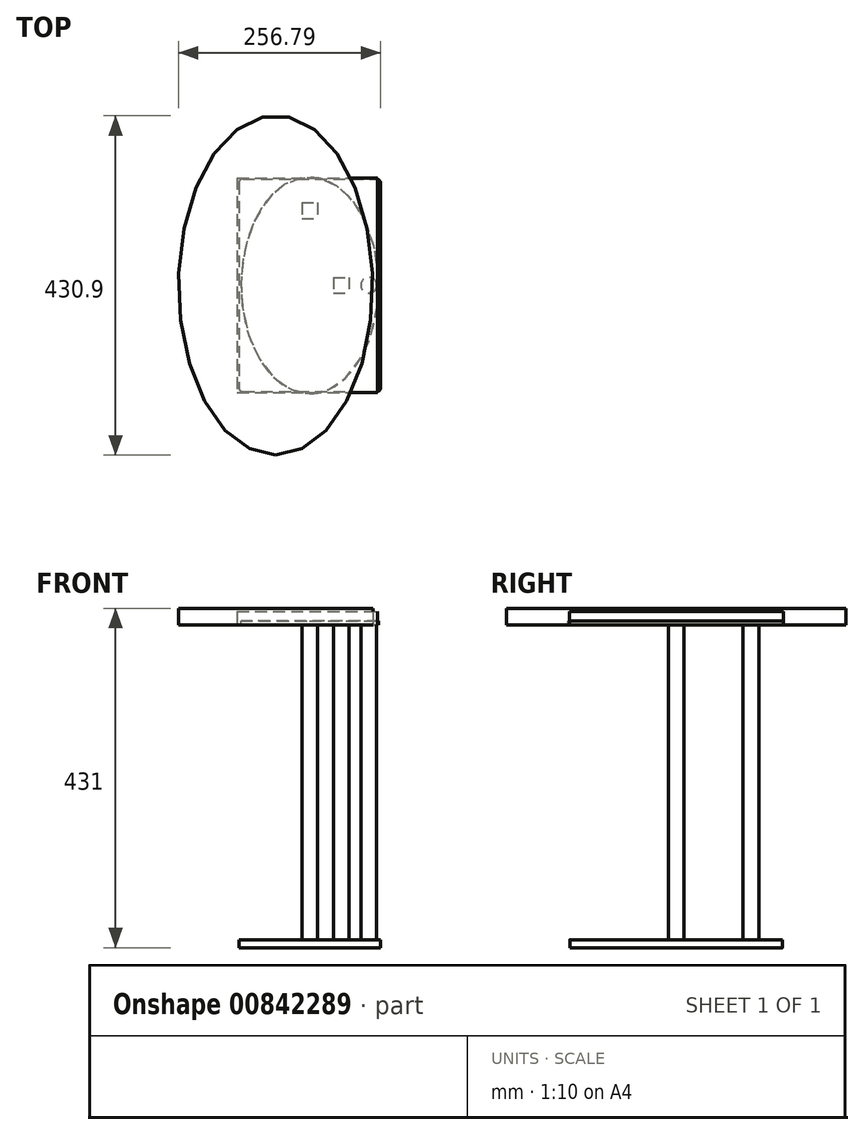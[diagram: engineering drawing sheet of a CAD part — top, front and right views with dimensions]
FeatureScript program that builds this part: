
annotation { "Feature Type Name" : "Feature", "Feature Type Description" : "" }
export const myFeature = defineFeature(function(context is Context, id is Id, definition is map)
    precondition{}
    {
        {
            var Q0;
            Q0=qCreatedBy(makeId("Top.planeOp"),FACE);
            var sketch = newSketch(context, id + "F0", { "sketchPlane" : qUnion([Q0])});
            skLineSegment(sketch, "E0.bottom", {"start": v(-180, 135) * mm, "end": v(0, 135) * mm});
            skLineSegment(sketch, "E0.top", {"start": v(-180, -135) * mm, "end": v(0, -135) * mm});
            skLineSegment(sketch, "E0.left", {"start": v(-180, 135) * mm, "end": v(-180, -135) * mm});
            skLineSegment(sketch, "E0.right", {"start": v(0, 135) * mm, "end": v(0, -135) * mm});
            skSolve(sketch);
        }
        {
            var Q0;
            Q0=makeQuery(id+"F0.imprint","IMPRINT",FACE,{"disambiguationData":[TD([[makeQuery(id+"F0.imprint","IMPRINT",EDGE,{"derivedFrom":sQuery(id+"F0.wireOp",EDGE,"E0.bottom")}),-1.0]])]});
            extrude(context, id + "F1", {"entities" : qUnion([Q0]), "depth" : 10 * mm, "offsetDistance" : 25 * mm});
        }
        {
            var Q0;
            Q0=makeQuery(id+"F1.opExtrude","SWEPT_EDGE",EDGE,{"disambiguationData":[OSD([sQuery(id+"F0.wireOp",EDGE,"E0.top"),sQuery(id+"F0.wireOp",EDGE,"E0.left")])]});
            var Q1;
            Q1=makeQuery(id+"F1.opExtrude","SWEPT_EDGE",EDGE,{"disambiguationData":[OSD([sQuery(id+"F0.wireOp",EDGE,"E0.top"),sQuery(id+"F0.wireOp",EDGE,"E0.right")])]});
            var Q2;
            Q2=makeQuery(id+"F1.opExtrude","SWEPT_EDGE",EDGE,{"disambiguationData":[OSD([sQuery(id+"F0.wireOp",EDGE,"E0.bottom"),sQuery(id+"F0.wireOp",EDGE,"E0.left")])]});
            var Q3;
            Q3=makeQuery(id+"F1.opExtrude","SWEPT_EDGE",EDGE,{"disambiguationData":[OSD([sQuery(id+"F0.wireOp",EDGE,"E0.bottom"),sQuery(id+"F0.wireOp",EDGE,"E0.right")])]});
            fillet(context, id + "F2", {"entities" : qUnion([Q0, Q1, Q2, Q3]), "radius" : 5 * mm, "tangentPropagation" : true, "allowEdgeOverflow" : false});
        }
        {
            var Q0;
            Q0=makeQuery(id+"F1.opExtrude","CAP_FACE",FACE,{"disambiguationData":[OSD([sQuery(id+"F0.wireOp",EDGE,"E0.bottom"),sQuery(id+"F0.wireOp",EDGE,"E0.top"),sQuery(id+"F0.wireOp",EDGE,"E0.left"),sQuery(id+"F0.wireOp",EDGE,"E0.right")])],"isStart":false});
            var sketch = newSketch(context, id + "F3", { "sketchPlane" : qUnion([Q0])});
            skCircle(sketch, "E1", {"center": v(-15, 0) * mm, "radius": 10 * mm});
            skSolve(sketch);
        }
        {
            var Q0;
            Q0=makeQuery(id+"F3.imprint","IMPRINT",FACE,{"disambiguationData":[TD([[makeQuery(id+"F3.imprint","IMPRINT",EDGE,{"derivedFrom":sQuery(id+"F3.wireOp",EDGE,"E1")}),1.0]])]});
            var Q1;
            Q1=sQuery(id+"F3.wireOp",EDGE,"E1");
            extrude(context, id + "F4", {"entities" : qUnion([Q0]), "surfaceEntities" : qUnion([Q1]), "depth" : 400 * mm, "offsetDistance" : 25 * mm});
        }
        {
            var Q0;
            Q0=qCreatedBy(makeId("Top.planeOp"),FACE);
            var sketch = newSketch(context, id + "F5", { "sketchPlane" : qUnion([Q0])});
            skEllipse(sketch, "E2", {"center": v(-135, 0) * mm, "majorRadius": 221.5 * mm, "minorRadius": 135 * mm, "majorAxis": v(0, -1)});
            skSolve(sketch);
        }
        {
            var Q0;
            Q0=sQuery(id+"F5.wireOp",EDGE,"E2");
            extrude(context, id + "F6", {"bodyType" : ToolBodyType.SURFACE, "surfaceEntities" : qUnion([Q0]), "depth" : 431 * mm, "offsetDistance" : 25 * mm, "hasSecondDirection" : true, "secondDirectionOppositeDirection" : false, "secondDirectionDepth" : (431 - 155) * mm});
        }
        {
            var Q0;
            Q0=makeQuery(id+"F4.opExtrude","CAP_FACE",FACE,{"disambiguationData":[OSD([sQuery(id+"F3.wireOp",EDGE,"E1")])],"isStart":false});
            var sketch = newSketch(context, id + "F7", { "sketchPlane" : qUnion([Q0])});
            skEllipse(sketch, "E3", {"center": v(-133.37, 0) * mm, "majorRadius": 215.45 * mm, "minorRadius": 123.43 * mm, "majorAxis": v(0, -1)});
            skSolve(sketch);
        }
        {
            var Q0;
            {var subQ0=sQuery(id+"F7.wireOp",EDGE,"E3");var subQ1=makeQuery(id+"F4.opExtrude","CAP_EDGE",EDGE,{"disambiguationData":[OSD([sQuery(id+"F3.wireOp",EDGE,"E1")])],"isStart":false});var subQ2=makeQuery(id+"F7.imprint","INTERSECT",VERTEX,{"disambiguationData":[OD(0.0)],"derivedFrom":[subQ1,subQ0]});Q0=makeQuery(id+"F7.imprint","IMPRINT",FACE,{"disambiguationData":[TD([[makeQuery(id+"F7.imprint","IMPRINT",EDGE,{"disambiguationData":[TD([[subQ2,1.0]])],"derivedFrom":subQ0}),1.0]])]});}
            var Q1;
            {var subQ0=sQuery(id+"F7.wireOp",EDGE,"E3");var subQ1=makeQuery(id+"F4.opExtrude","CAP_EDGE",EDGE,{"disambiguationData":[OSD([sQuery(id+"F3.wireOp",EDGE,"E1")])],"isStart":false});var subQ2=makeQuery(id+"F7.imprint","INTERSECT",VERTEX,{"disambiguationData":[OD(0.0)],"derivedFrom":[subQ1,subQ0]});Q1=makeQuery(id+"F7.imprint","IMPRINT",FACE,{"disambiguationData":[TD([[makeQuery(id+"F7.imprint","IMPRINT",EDGE,{"disambiguationData":[TD([[subQ2,-1.0]])],"derivedFrom":subQ0}),1.0]])]});}
            var Q2;
            Q2=sQuery(id+"F7.wireOp",EDGE,"E3");
            var Q3;
            Q3=makeQuery(id+"F6.opExtrude","SWEPT_FACE",FACE,{"disambiguationData":[OSD([sQuery(id+"F5.wireOp",EDGE,"E2")])]});
            extrude(context, id + "F8", {"entities" : qUnion([Q0, Q1]), "surfaceEntities" : qUnion([Q2]), "depth" : 21 * mm, "endBoundEntityFace" : qUnion([Q3]), "offsetDistance" : 25 * mm});
        }
        {
            var Q0;
            Q0=qCreatedBy(makeId("Top.planeOp"),FACE);
            var sketch = newSketch(context, id + "F9", { "sketchPlane" : qUnion([Q0])});
            skLineSegment(sketch, "E4.bottom", {"start": v(-190, 145) * mm, "end": v(0, 145) * mm});
            skLineSegment(sketch, "E4.top", {"start": v(-190, -145) * mm, "end": v(0, -145) * mm});
            skLineSegment(sketch, "E4.left", {"start": v(-190, 145) * mm, "end": v(-190, -145) * mm});
            skLineSegment(sketch, "E4.right", {"start": v(0, 145) * mm, "end": v(0, -145) * mm});
            skSolve(sketch);
        }
        {
            var Q0;
            Q0=makeQuery(id+"F9.imprint","IMPRINT",FACE,{"disambiguationData":[TD([[makeQuery(id+"F9.imprint","IMPRINT",EDGE,{"derivedFrom":sQuery(id+"F9.wireOp",EDGE,"E4.bottom")}),-1.0]])]});
            var Q1;
            Q1 = qConstructionFilter(qBodyType(qCreatedBy(id + "F9" ,EDGE), BodyType.WIRE), ConstructionObject.NO);
            extrude(context, id + "F10", {"entities" : qUnion([Q0]), "bodyType" : ToolBodyType.SURFACE, "surfaceEntities" : qUnion([Q1]), "depth" : 428 * mm, "offsetDistance" : 25 * mm, "hasSecondDirection" : true, "secondDirectionOppositeDirection" : false, "secondDirectionDepth" : (428 - 190) * mm});
        }
        {
            var Q0;
            Q0=makeQuery(id+"F4.opExtrude","CAP_FACE",FACE,{"disambiguationData":[OSD([sQuery(id+"F3.wireOp",EDGE,"E1")])],"isStart":false});
            var sketch = newSketch(context, id + "F11", { "sketchPlane" : qUnion([Q0])});
            skLineSegment(sketch, "E5.bottom", {"start": v(-182.39, 136.37) * mm, "end": v(-3.83, 136.37) * mm});
            skLineSegment(sketch, "E5.top", {"start": v(-182.39, -135.82) * mm, "end": v(-3.83, -135.82) * mm});
            skLineSegment(sketch, "E5.left", {"start": v(-182.39, 136.37) * mm, "end": v(-182.39, -135.82) * mm});
            skLineSegment(sketch, "E5.right", {"start": v(-3.83, 136.37) * mm, "end": v(-3.83, -135.82) * mm});
            skSolve(sketch);
        }
        {
            var Q0;
            Q0=makeQuery(id+"F11.imprint","IMPRINT",FACE,{"disambiguationData":[TD([[makeQuery(id+"F11.imprint","IMPRINT",EDGE,{"derivedFrom":sQuery(id+"F11.wireOp",EDGE,"E5.bottom")}),-1.0]])]});
            var Q1;
            Q1=makeQuery(id+"F11.imprint","IMPRINT",FACE,{"disambiguationData":[TD([[makeQuery(id+"F11.imprint","IMPRINT",EDGE,{"derivedFrom":makeQuery(id+"F4.opExtrude","CAP_EDGE",EDGE,{"disambiguationData":[OSD([sQuery(id+"F3.wireOp",EDGE,"E1")])],"isStart":false})}),1.0]])]});
            extrude(context, id + "F12", {"entities" : qUnion([Q0, Q1]), "depth" : 17 * mm, "offsetDistance" : 25 * mm});
        }
        {
            var Q0;
            Q0=qCreatedBy(makeId("Top.planeOp"),FACE);
            cPlane(context, id + "F13", {"entities" : qUnion([Q0]), "cplaneType" : CPlaneType.OFFSET, "offset" : 247 * mm, "width" : 150 * mm, "height" : 150 * mm});
        }
        {
            var Q0;
            Q0=qCreatedBy(id+"F13.planeOp",FACE);
            var sketch = newSketch(context, id + "F14", { "sketchPlane" : qUnion([Q0])});
            skLineSegment(sketch, "E6.bottom", {"start": v(-190, 145) * mm, "end": v(0, 145) * mm});
            skLineSegment(sketch, "E6.top", {"start": v(-190, -145) * mm, "end": v(0, -145) * mm});
            skLineSegment(sketch, "E6.left", {"start": v(-190, 145) * mm, "end": v(-190, -145) * mm});
            skLineSegment(sketch, "E6.right", {"start": v(0, 145) * mm, "end": v(0, -145) * mm});
            skSolve(sketch);
        }
        {
            var Q0;
            Q0=qCreatedBy(makeId("Top.planeOp"),FACE);
            cPlane(context, id + "F15", {"entities" : qUnion([Q0]), "cplaneType" : CPlaneType.OFFSET, "offset" : 430 * mm, "width" : 150 * mm, "height" : 150 * mm});
        }
        {
            var Q0;
            Q0=qCreatedBy(id+"F15.planeOp",FACE);
            var sketch = newSketch(context, id + "F16", { "sketchPlane" : qUnion([Q0])});
            skLineSegment(sketch, "E7.bottom", {"start": v(-110, 81.54) * mm, "end": v(0, 81.54) * mm});
            skLineSegment(sketch, "E7.top", {"start": v(-110, -94.46) * mm, "end": v(0, -94.46) * mm});
            skLineSegment(sketch, "E7.left", {"start": v(-110, 81.54) * mm, "end": v(-110, -94.46) * mm});
            skLineSegment(sketch, "E7.right", {"start": v(0, 81.54) * mm, "end": v(0, -94.46) * mm});
            skSolve(sketch);
        }
        {
            var Q1;
            Q1=makeQuery(id+"F14.imprint","IMPRINT",FACE,{"disambiguationData":[TD([[makeQuery(id+"F14.imprint","IMPRINT",EDGE,{"derivedFrom":sQuery(id+"F14.wireOp",EDGE,"E6.bottom")}),-1.0]])]});
            var Q2;
            Q2=makeQuery(id+"F16.imprint","IMPRINT",FACE,{"disambiguationData":[TD([[makeQuery(id+"F16.imprint","IMPRINT",EDGE,{"derivedFrom":sQuery(id+"F16.wireOp",EDGE,"E7.bottom")}),-1.0]])]});
            var Q3;
            Q3=makeQuery(id+"F14.imprint","IMPRINT",FACE,{"disambiguationData":[TD([[makeQuery(id+"F14.imprint","IMPRINT",EDGE,{"derivedFrom":sQuery(id+"F14.wireOp",EDGE,"E6.bottom")}),-1.0]])]});
            var Q4;
            Q4=makeQuery(id+"F16.imprint","IMPRINT",FACE,{"disambiguationData":[TD([[makeQuery(id+"F16.imprint","IMPRINT",EDGE,{"derivedFrom":sQuery(id+"F16.wireOp",EDGE,"E7.bottom")}),-1.0]])]});
            loft(context, id + "F17", {"bodyType" : ToolBodyType.SURFACE, "operationType" : NewBodyOperationType.ADD, "sheetProfilesArray" : [{ "sheetProfileEntities" : qUnion([Q1]) }, { "sheetProfileEntities" : qUnion([Q2]) }], "wireProfilesArray" : [{ "wireProfileEntities" : qUnion([Q3]) }, { "wireProfileEntities" : qUnion([Q4]) }]});
        }
        {
            var Q0;
            Q0=makeQuery(id+"F3.imprint","IMPRINT",FACE,{"disambiguationData":[TD([[makeQuery(id+"F3.imprint","IMPRINT",EDGE,{"derivedFrom":sQuery(id+"F3.wireOp",EDGE,"E1")}),-1.0]])]});
            var sketch = newSketch(context, id + "F18", { "sketchPlane" : qUnion([Q0])});
            skLineSegment(sketch, "E8.bottom", {"start": v(-60, 10) * mm, "end": v(-40, 10) * mm});
            skLineSegment(sketch, "E8.top", {"start": v(-60, -10) * mm, "end": v(-40, -10) * mm});
            skLineSegment(sketch, "E8.left", {"start": v(-60, 10) * mm, "end": v(-60, -10) * mm});
            skLineSegment(sketch, "E8.right", {"start": v(-40, 10) * mm, "end": v(-40, -10) * mm});
            skSolve(sketch);
        }
        {
            var Q0;
            Q0 = qSketchRegion(id + "F18", true);
            extrude(context, id + "F19", {"entities" : qUnion([Q0]), "depth" : 400 * mm, "offsetDistance" : 25 * mm});
        }
        {
            var Q0;
            Q0=qCreatedBy(id+"F15.planeOp",FACE);
            var sketch = newSketch(context, id + "F20", { "sketchPlane" : qUnion([Q0])});
            skEllipse(sketch, "E9", {"center": v(-90, 0) * mm, "majorRadius": 152.5 * mm, "minorRadius": 105 * mm, "majorAxis": v(0, -1)});
            skSolve(sketch);
        }
        {
            var Q0;
            Q0=sQuery(id+"F20.wireOp",EDGE,"E9");
            extrude(context, id + "F21", {"bodyType" : ToolBodyType.SURFACE, "surfaceEntities" : qUnion([Q0]), "oppositeDirection" : true, "depth" : 140 * mm, "offsetDistance" : 25 * mm});
        }
        {
            var Q0;
            Q0=qCreatedBy(id+"F15.planeOp",FACE);
            var sketch = newSketch(context, id + "F22", { "sketchPlane" : qUnion([Q0])});
            skEllipse(sketch, "E10", {"center": v(-90, 0) * mm, "majorRadius": 137.5 * mm, "minorRadius": 87.5 * mm, "majorAxis": v(0, -1)});
            skSolve(sketch);
        }
        {
            var Q0;
            Q0=makeQuery(id+"F22.imprint","IMPRINT",FACE,{"disambiguationData":[TD([[makeQuery(id+"F22.imprint","IMPRINT",EDGE,{"derivedFrom":sQuery(id+"F22.wireOp",EDGE,"E10")}),1.0]])]});
            var Q1;
            Q1=sQuery(id+"F22.wireOp",EDGE,"E10");
            extrude(context, id + "F23", {"entities" : qUnion([Q0]), "surfaceEntities" : qUnion([Q1]), "oppositeDirection" : true, "depth" : 20 * mm, "offsetDistance" : 25 * mm, "hasSecondDirection" : true, "secondDirectionOppositeDirection" : false, "secondDirectionDepth" : -15 * mm});
        }
        {
            var Q0;
            Q0=makeQuery(id+"F1.opExtrude","CAP_FACE",FACE,{"disambiguationData":[OSD([sQuery(id+"F0.wireOp",EDGE,"E0.bottom"),sQuery(id+"F0.wireOp",EDGE,"E0.top"),sQuery(id+"F0.wireOp",EDGE,"E0.left"),sQuery(id+"F0.wireOp",EDGE,"E0.right")])],"isStart":false});
            var sketch = newSketch(context, id + "F24", { "sketchPlane" : qUnion([Q0])});
            skLineSegment(sketch, "E11.bottom", {"start": v(-100, 105) * mm, "end": v(-80, 105) * mm});
            skLineSegment(sketch, "E11.top", {"start": v(-100, 85) * mm, "end": v(-80, 85) * mm});
            skLineSegment(sketch, "E11.left", {"start": v(-100, 105) * mm, "end": v(-100, 85) * mm});
            skLineSegment(sketch, "E11.right", {"start": v(-80, 105) * mm, "end": v(-80, 85) * mm});
            skSolve(sketch);
        }
        {
            var Q0;
            Q0 = qSketchRegion(id + "F24", true);
            extrude(context, id + "F25", {"entities" : qUnion([Q0]), "depth" : 400 * mm, "offsetDistance" : 25 * mm});
        }
    });
